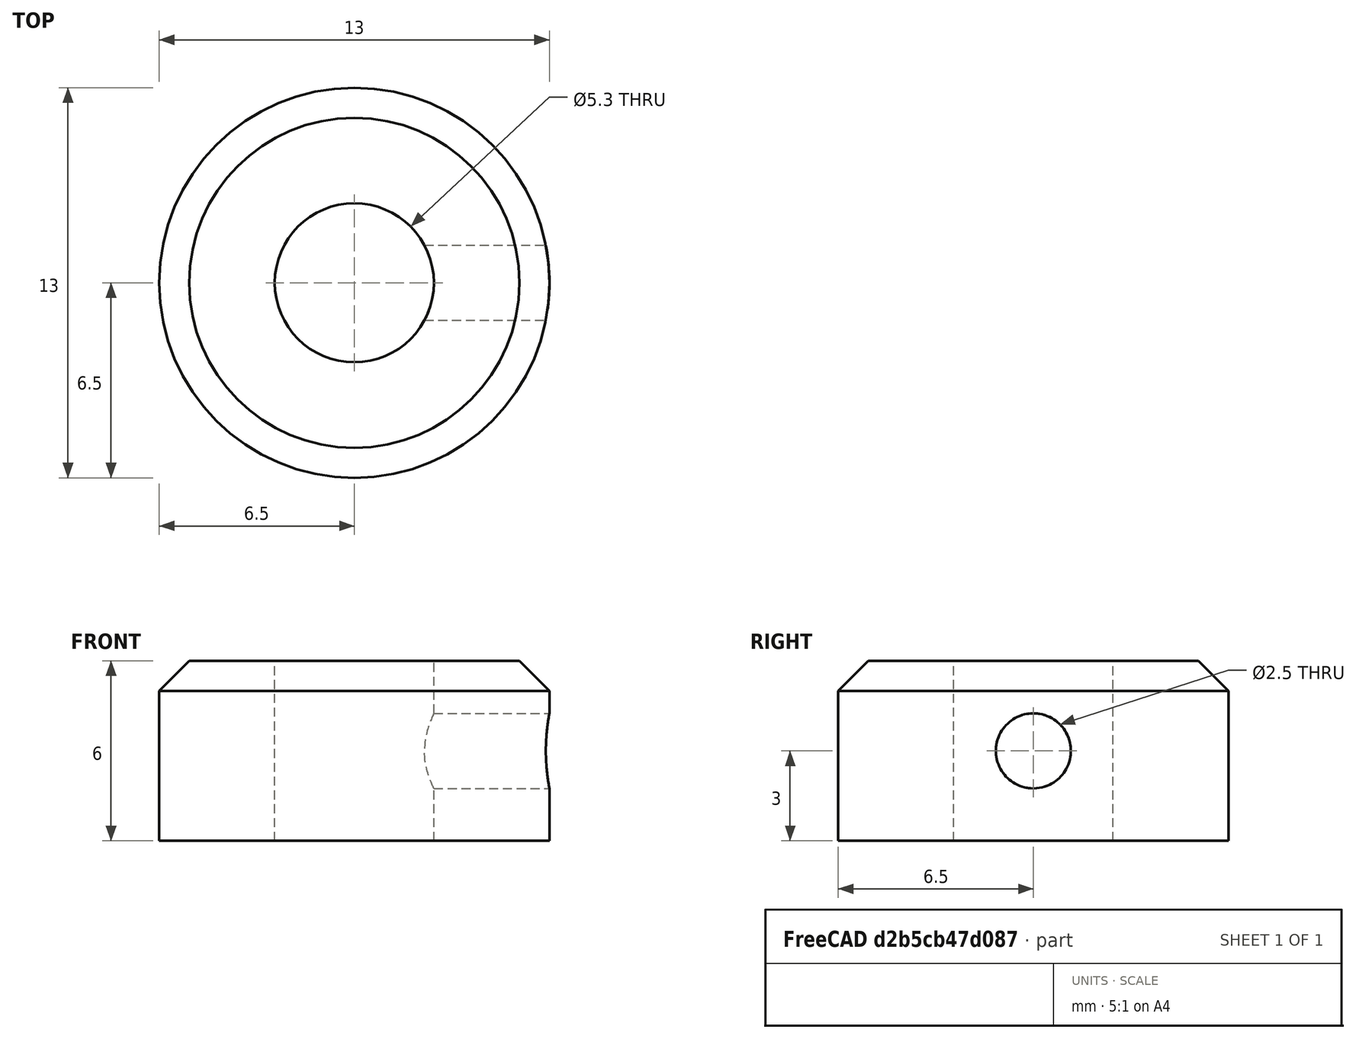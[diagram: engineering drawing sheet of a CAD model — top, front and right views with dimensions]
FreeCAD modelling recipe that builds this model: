
FCSTD DOCUMENT  (FreeCAD 0.16R6712 (Git))
Label: tpge-shaftcollar
License: CreativeCommons Attribution-ShareAlike
LicenseURL: http://creativecommons.org/licenses/by-sa/4.0/
objects: Part::Cylinder×3, Part::Cut×2, Mesh::Feature×1, Part::Chamfer×1
note: 6 computed .brp shape members not serialized (recipe doc carries the construction recipe); baked Part::Feature solids carry a one-line shape summary decoded from their .brp

FEATURE [Mesh::Feature] tpge_shaftcollar  label="tpge-shaftcollar"
FEATURE [Part::Cylinder] Cylinder  label="Zylinder"
  Angle = 360
  Height = 6
  Radius = 6.5
FEATURE [Part::Cylinder] Cylinder001  label="Zylinder001"
  Angle = 360
  Height = 10
  Placement = pos=(0,0,-2) rot=(0,0,1;0rad)
  Radius = 2.65
FEATURE [Part::Cylinder] Cylinder002  label="Zylinder002"
  Angle = 360
  Height = 10
  Placement = pos=(0,0,3) rot=(0,1,0;1.5708rad)
  Radius = 1.25
FEATURE [Part::Cut] Cut
  Base = -> Cylinder
  Tool = -> Cylinder001
FEATURE [Part::Cut] Cut001
  Base = -> Cut
  Tool = -> Cylinder002
FEATURE [Part::Chamfer] Chamfer
  Base = -> Cut001
  Edges = 1 edges r=1: [Edge8]
